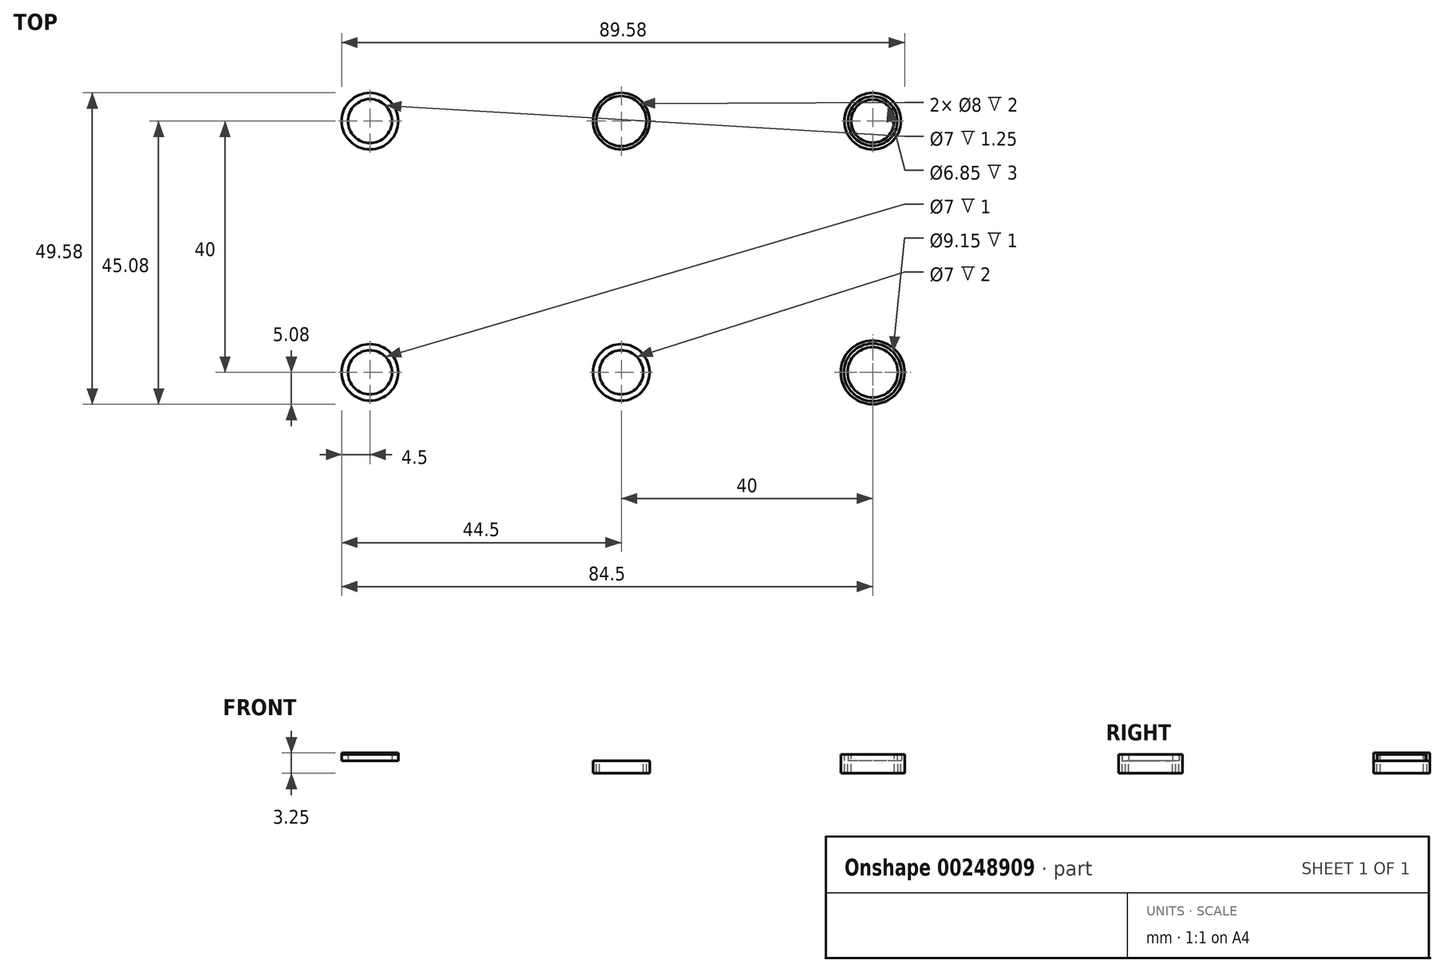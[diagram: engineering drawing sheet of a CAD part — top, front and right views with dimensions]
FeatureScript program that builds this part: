
annotation { "Feature Type Name" : "Feature", "Feature Type Description" : "" }
export const myFeature = defineFeature(function(context is Context, id is Id, definition is map)
    precondition{}
    {
        {
            var Q0;
            Q0=qCreatedBy(makeId("Top.planeOp"),FACE);
            var sketch = newSketch(context, id + "F0", { "sketchPlane" : qUnion([Q0])});
            skCircle(sketch, "E0", {"center": v(-20, 20) * mm, "radius": 4.5 * mm});
            skCircle(sketch, "E1", {"center": v(20, 20) * mm, "radius": 3.92 * mm});
            skCircle(sketch, "E2", {"center": v(20, -20) * mm, "radius": 4 * mm});
            skCircle(sketch, "E3", {"center": v(-20, -20) * mm, "radius": 4.5 * mm});
            skCircle(sketch, "E4", {"center": v(-20, 20) * mm, "radius": 4 * mm});
            skCircle(sketch, "E5", {"center": v(20, 20) * mm, "radius": 4.5 * mm});
            skCircle(sketch, "E6", {"center": v(20, 20) * mm, "radius": 3.42 * mm});
            skCircle(sketch, "E7", {"center": v(20, -20) * mm, "radius": 4.58 * mm});
            skCircle(sketch, "E8", {"center": v(20, -20) * mm, "radius": 5.07 * mm});
            skCircle(sketch, "E9", {"center": v(-20, -20) * mm, "radius": 3.5 * mm});
            skCircle(sketch, "E10", {"center": v(-60, -20) * mm, "radius": 4.5 * mm});
            skCircle(sketch, "E11", {"center": v(-60, -20) * mm, "radius": 3.5 * mm});
            skCircle(sketch, "E12", {"center": v(-60, 20) * mm, "radius": 4.5 * mm});
            skCircle(sketch, "E13", {"center": v(-60, 20) * mm, "radius": 3.5 * mm});
            skSolve(sketch);
        }
        {
            var Q0;
            Q0=makeQuery(id+"F0.imprint","IMPRINT",FACE,{"disambiguationData":[TD([[makeQuery(id+"F0.imprint","IMPRINT",EDGE,{"derivedFrom":sQuery(id+"F0.wireOp",EDGE,"E0")}),1.0]])]});
            var Q1;
            Q1=makeQuery(id+"F0.imprint","IMPRINT",FACE,{"disambiguationData":[TD([[makeQuery(id+"F0.imprint","IMPRINT",EDGE,{"derivedFrom":sQuery(id+"F0.wireOp",EDGE,"E3")}),1.0]])]});
            var Q2;
            Q2=makeQuery(id+"F0.imprint","IMPRINT",FACE,{"disambiguationData":[TD([[makeQuery(id+"F0.imprint","IMPRINT",EDGE,{"derivedFrom":sQuery(id+"F0.wireOp",EDGE,"E2")}),-1.0]])]});
            var Q3;
            Q3=makeQuery(id+"F0.imprint","IMPRINT",FACE,{"disambiguationData":[TD([[makeQuery(id+"F0.imprint","IMPRINT",EDGE,{"derivedFrom":sQuery(id+"F0.wireOp",EDGE,"E7")}),-1.0]])]});
            var Q4;
            Q4=makeQuery(id+"F0.imprint","IMPRINT",FACE,{"disambiguationData":[TD([[makeQuery(id+"F0.imprint","IMPRINT",EDGE,{"derivedFrom":sQuery(id+"F0.wireOp",EDGE,"E1")}),1.0]])]});
            var Q5;
            Q5=makeQuery(id+"F0.imprint","IMPRINT",FACE,{"disambiguationData":[TD([[makeQuery(id+"F0.imprint","IMPRINT",EDGE,{"derivedFrom":sQuery(id+"F0.wireOp",EDGE,"E1")}),-1.0]])]});
            extrude(context, id + "F1", {"entities" : qUnion([Q0, Q1, Q2, Q3, Q4, Q5]), "oppositeDirection" : true, "depth" : 2 * mm});
        }
        {
            var Q0;
            Q0=makeQuery(id+"F0.imprint","IMPRINT",FACE,{"disambiguationData":[TD([[makeQuery(id+"F0.imprint","IMPRINT",EDGE,{"derivedFrom":sQuery(id+"F0.wireOp",EDGE,"E1")}),1.0]])]});
            var Q1;
            Q1=makeQuery(id+"F0.imprint","IMPRINT",FACE,{"disambiguationData":[TD([[makeQuery(id+"F0.imprint","IMPRINT",EDGE,{"derivedFrom":sQuery(id+"F0.wireOp",EDGE,"E7")}),-1.0]])]});
            extrude(context, id + "F2", {"entities" : qUnion([Q0, Q1]), "operationType" : NewBodyOperationType.ADD, "depth" : 1 * mm});
        }
        {
            var Q0;
            Q0=makeQuery(id+"F0.imprint","IMPRINT",FACE,{"disambiguationData":[TD([[makeQuery(id+"F0.imprint","IMPRINT",EDGE,{"derivedFrom":sQuery(id+"F0.wireOp",EDGE,"E12")}),1.0]])]});
            extrude(context, id + "F3", {"entities" : qUnion([Q0]), "depth" : 1.25 * mm});
        }
        {
            var Q0;
            Q0=makeQuery(id+"F0.imprint","IMPRINT",FACE,{"disambiguationData":[TD([[makeQuery(id+"F0.imprint","IMPRINT",EDGE,{"derivedFrom":sQuery(id+"F0.wireOp",EDGE,"E10")}),1.0]])]});
            extrude(context, id + "F4", {"entities" : qUnion([Q0]), "depth" : 1 * mm});
        }
    });
